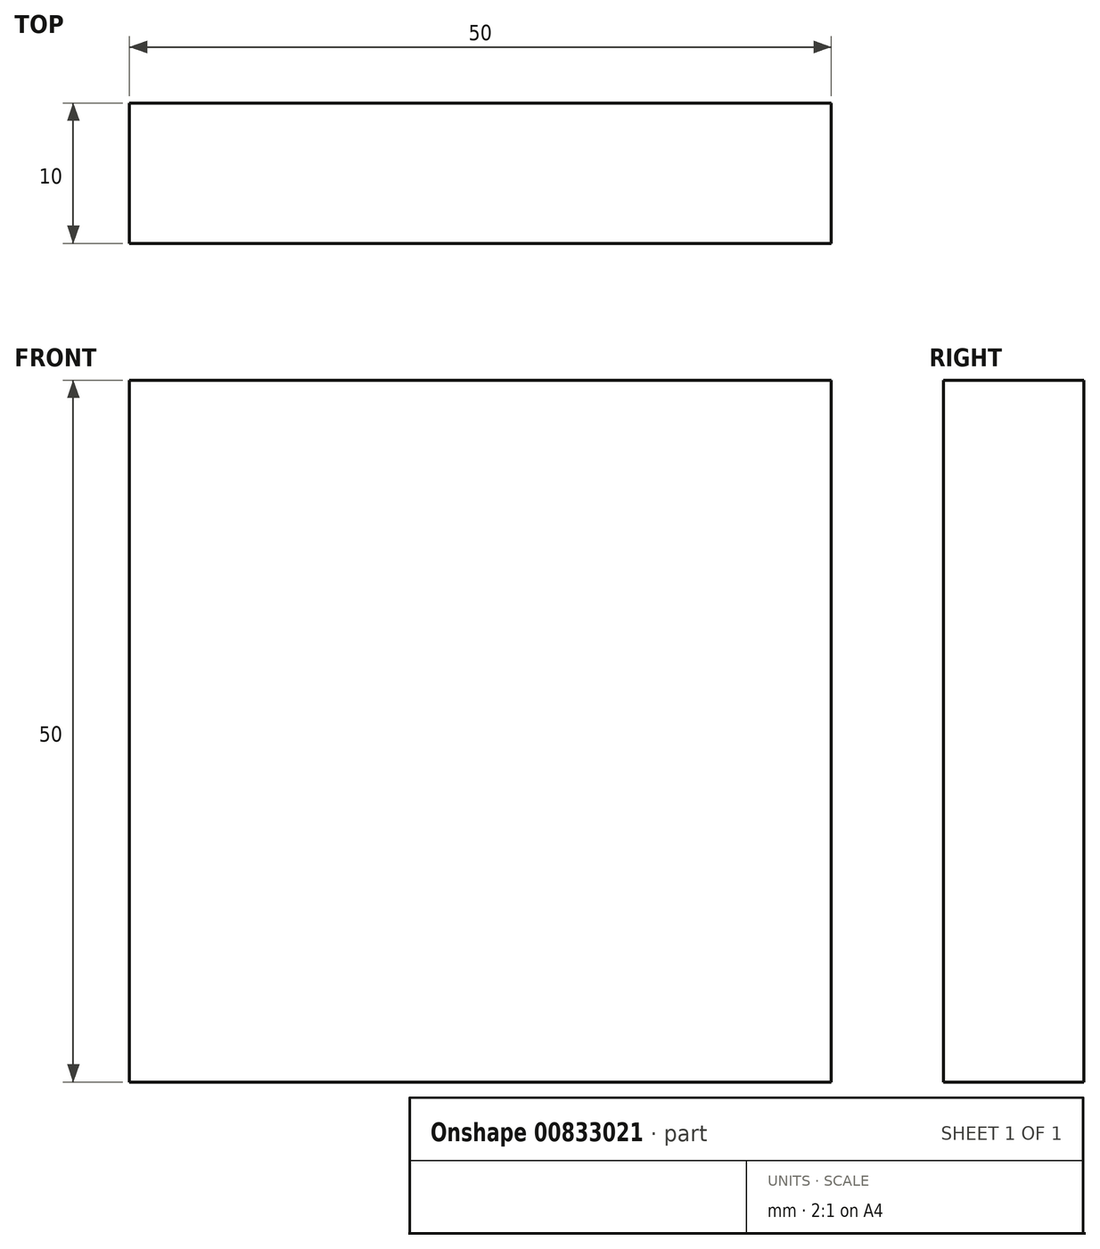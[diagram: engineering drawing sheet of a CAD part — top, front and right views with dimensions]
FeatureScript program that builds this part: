
annotation { "Feature Type Name" : "Feature", "Feature Type Description" : "" }
export const myFeature = defineFeature(function(context is Context, id is Id, definition is map)
    precondition{}
    {
        {
            var Q0;
            Q0=qCreatedBy(makeId("Front.planeOp"),FACE);
            var sketch = newSketch(context, id + "F0", { "sketchPlane" : qUnion([Q0])});
            skLineSegment(sketch, "E0.bottom", {"start": v(25, 25) * mm, "end": v(-25, 25) * mm});
            skLineSegment(sketch, "E0.top", {"start": v(25, -25) * mm, "end": v(-25, -25) * mm});
            skLineSegment(sketch, "E0.left", {"start": v(25, 25) * mm, "end": v(25, -25) * mm});
            skLineSegment(sketch, "E0.right", {"start": v(-25, 25) * mm, "end": v(-25, -25) * mm});
            skPoint(sketch, "E0.middle", {"position": v(0, 0) * mm});
            skSolve(sketch);
        }
        {
            var Q0;
            Q0=makeQuery(id+"F0.imprint","IMPRINT",FACE,{"disambiguationData":[TD([[makeQuery(id+"F0.imprint","IMPRINT",EDGE,{"derivedFrom":sQuery(id+"F0.wireOp",EDGE,"E0.bottom")}),1.0]])]});
            extrude(context, id + "F1", {"entities" : qUnion([Q0]), "depth" : 10 * mm, "offsetDistance" : 25 * mm});
        }
    });
